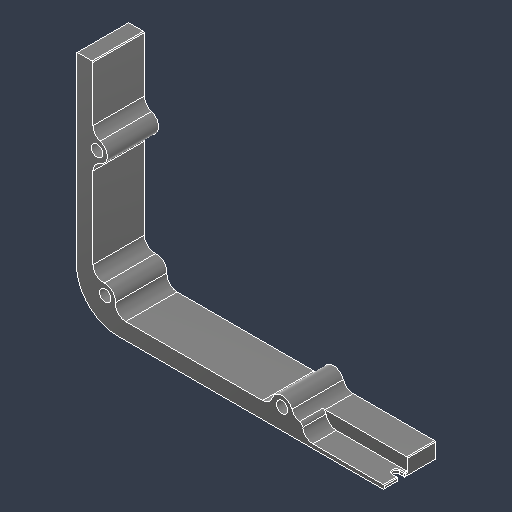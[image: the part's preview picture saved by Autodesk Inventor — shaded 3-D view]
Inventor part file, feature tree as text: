
AUTODESK INVENTOR PART (.ipt)
format: ipt  version: 2023.4 (Build 274418000, 418)  size: 214,528 bytes
history: native  units: mm
features: fillet x8, sketch x5, extrude x4, hole x1
ambient origin geometry x8: Origin, YZ Plane, XZ Plane, XY Plane, X Axis, Y Axis, Z Axis, Center Point
bodies: Solid1 (feature_tree)
feature tree (18):
  extrude  "Extrusion1"  Depth=109.6mm
  fillet  "Fillet1"  Radius=8.0mm
  fillet  "Fillet2"  Radius=8.0mm
  extrude  "Extrusion2"  Depth=25.0mm
  hole  "Hole1"  [1 undecoded]
  fillet  "Fillet3"  Radius=10.0mm
  fillet  "Fillet4"  Radius=14.0mm
  extrude  "Extrusion3"  Depth=73.0mm
  extrude  "Extrusion4"  Depth=10.0mm
  fillet  "Fillet5"  Radius=25.0mm
  fillet  "Fillet6"  Radius=5.0mm
  fillet  "Fillet7"  Radius=0.4mm
  fillet  "Fillet8"  Radius=110.0mm
  sketch  "Sketch1"  dims[d0=149.6mm d1=109.6mm d2=8.0mm d3=8.0mm]
  sketch  "Sketch2"  dims[d4=25.0mm d5=0.0mm d6=12.0mm]
  sketch  "Sketch3"  dims[d7=20.0mm d8=10.0mm d9=10.0mm d10=14.0mm]
  sketch  "Sketch4"  dims[d11=14.0mm d12=73.0mm]
  sketch  "Sketch5"  dims[d13=100.0mm d14=10.0mm d15=25.0mm d16=0.0mm d17=5.6mm d18=6.0mm d19=7.5mm d20=2.0mm d21=90.0deg d22=15.0mm d23=0.0mm d24=5.0mm d25=0.4mm d26=110.0mm d27=13.6mm d29=6.0mm d30=0.0mm d31=0.4mm d32=3.2mm d33=16.6mm d35=9.2mm d36=0.0mm d37=0.0mm d38=0.4mm d39=0.4mm d40=2.0mm d41=5.0mm]
note: 1 required parameter value undecoded (feature->parameter linkage not recoverable at this tier; creation-order binding heuristic only, values carry confidence <= 0.55)
